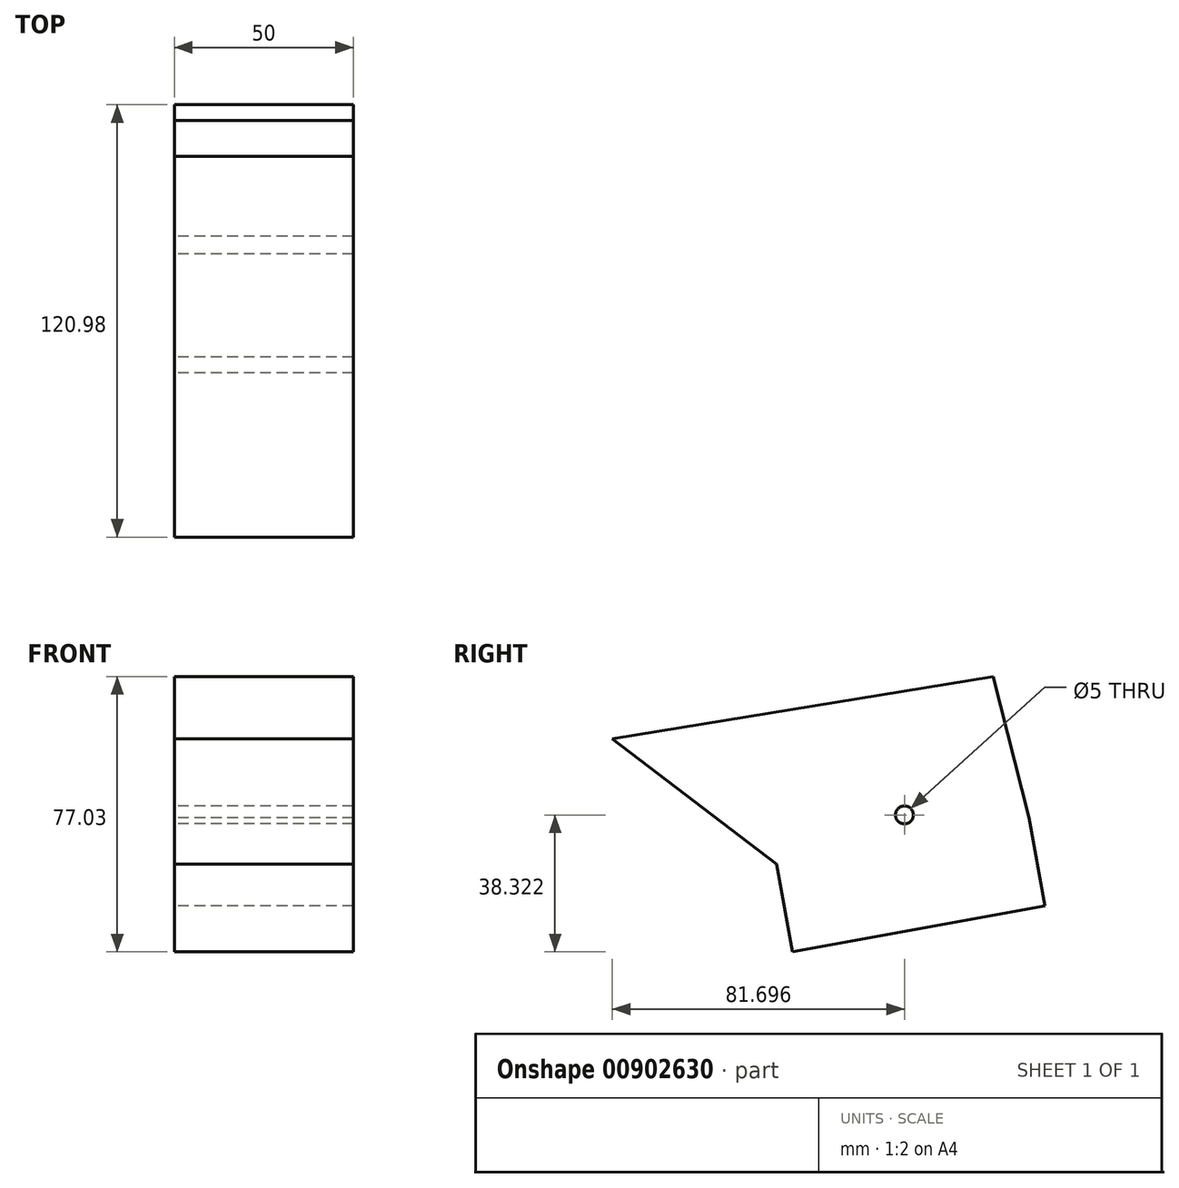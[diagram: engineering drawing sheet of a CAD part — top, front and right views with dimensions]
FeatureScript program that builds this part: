
annotation { "Feature Type Name" : "Feature", "Feature Type Description" : "" }
export const myFeature = defineFeature(function(context is Context, id is Id, definition is map)
    precondition{}
    {
        {
            var Q0;
            Q0=qCreatedBy(makeId("Right.planeOp"),FACE);
            var sketch = newSketch(context, id + "F0", { "sketchPlane" : qUnion([Q0])});
            skLineSegment(sketch, "E0", {"start": v(-58.34, 41.82) * mm, "end": v(48.18, 59.24) * mm});
            skLineSegment(sketch, "E1", {"start": v(48.18, 59.24) * mm, "end": v(58.16, 19.69) * mm});
            skLineSegment(sketch, "E2", {"start": v(58.16, 19.69) * mm, "end": v(-12.43, 6.8) * mm});
            skLineSegment(sketch, "E3", {"start": v(-12.43, 6.8) * mm, "end": v(-58.34, 41.82) * mm});
            skSolve(sketch);
        }
        {
            var Q0;
            Q0=makeQuery(id+"F0.imprint","IMPRINT",FACE,{"disambiguationData":[TD([[makeQuery(id+"F0.imprint","IMPRINT",EDGE,{"derivedFrom":sQuery(id+"F0.wireOp",EDGE,"E0")}),-1.0]])]});
            extrude(context, id + "F1", {"entities" : qUnion([Q0]), "depth" : 25 * mm, "offsetDistance" : 25 * mm, "hasSecondDirection" : true, "secondDirectionOppositeDirection" : true, "secondDirectionDepth" : 25 * mm});
        }
        {
            var Q0;
            Q0=makeQuery(id+"F1.opExtrude","SWEPT_FACE",FACE,{"disambiguationData":[OSD([sQuery(id+"F0.wireOp",EDGE,"E2")])]});
            extrude(context, id + "F2", {"entities" : qUnion([Q0]), "operationType" : NewBodyOperationType.ADD, "depth" : 25 * mm, "offsetDistance" : 25 * mm});
        }
        {
            var Q0;
            {var subQ0=sQuery(id+"F0.wireOp",EDGE,"E2");Q0=makeQuery(id+"F2.boolean.opBoolean","MERGE",FACE,{"derivedFrom":[makeQuery(id+"F1.opExtrude","CAP_FACE",FACE,{"disambiguationData":[OSD([sQuery(id+"F0.wireOp",EDGE,"E0"),sQuery(id+"F0.wireOp",EDGE,"E1"),subQ0,sQuery(id+"F0.wireOp",EDGE,"E3")])],"isStart":true}),makeQuery(id+"F2.opExtrude","SWEPT_FACE",FACE,{"disambiguationData":[OSD([subQ0]),TDD([makeQuery(id+"F1.opExtrude","CAP_EDGE",EDGE,{"disambiguationData":[OSD([subQ0])],"isStart":true})])]})]});}
            var sketch = newSketch(context, id + "F3", { "sketchPlane" : qUnion([Q0])});
            skPoint(sketch, "E4", {"position": v(-23.36, 20.53) * mm});
            skSolve(sketch);
        }
        {
            var Q0;
            Q0=sQuery(id+"F3.wireOp",VERTEX,"E4");
            var Q1;
            Q1=makeQuery(id+"F1.opExtrude","SWEPT_BODY",BODY,{"disambiguationData":[OSD([sQuery(id+"F0.wireOp",EDGE,"E0"),sQuery(id+"F0.wireOp",EDGE,"E1"),sQuery(id+"F0.wireOp",EDGE,"E2"),sQuery(id+"F0.wireOp",EDGE,"E3")])]});
            hole(context, id + "F4", {"style" : HoleStyle.SIMPLE, "endStyle" : HoleEndStyle.THROUGH, "holeDiameter" : 5 * mm, "majorDiameter" : 5 * mm, "isTappedThrough" : true, "tappedDepth" : 12 * mm, "tapClearance" : 3, "locations" : qUnion([Q0]), "scope" : qUnion([Q1])});
        }
    });
